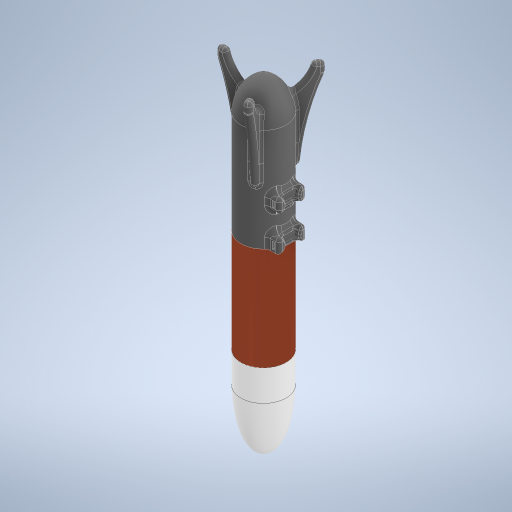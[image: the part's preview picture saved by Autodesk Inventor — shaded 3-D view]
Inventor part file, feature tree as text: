
AUTODESK INVENTOR PART (.ipt)
format: ipt  version: 2023 (Build 270158030, 158C)  size: 1,821,184 bytes
history: native  units: mm
features: fillet x17, sketch x15, extrude x14, other x12, plane x4, revolve x3, pattern_circular x2, pattern_linear x1, mirror x1, chamfer x1
ambient origin geometry x8: Origin, YZ Plane, XZ Plane, XY Plane, X Axis, Y Axis, Z Axis, Center Point
bodies: Body1 (feature_tree), Body2 (feature_tree), Body3 (feature_tree), Body4 (feature_tree), Body5 (feature_tree), Body6 (feature_tree), Body7 (feature_tree)
feature tree (70):
  other  "stage-one"
  extrude  "body-tube"  Depth=3.0mm
  extrude  "Extrusion2"  Depth=20.0mm
  extrude  "Extrusion3"  Depth=10.0mm
  plane  "Work Plane2"
  plane  "Work Plane4"
  extrude  "Extrusion4"  Depth=12.5mm
  plane  "Work Plane6"
  pattern_linear  "Rectangular Pattern1"  Count1=2  [1 undecoded]
  extrude  "Extrusion7"  Depth=6.0mm
  other  "Work Point2"
  revolve  "Revolution2"  [1 undecoded]
  mirror  "Mirror1"
  extrude  "Extrusion5"  Depth=4.0mm
  fillet  "Fillet1"  [1 undecoded]
  fillet  "Fillet2"  Radius=30.0mm
  fillet  "Fillet3"  Radius=200.0mm
  chamfer  "Chamfer1"  Distance=20.0mm
  fillet  "Fillet4"  Radius=7.0mm
  fillet  "Fillet5"  Radius=7.0mm
  fillet  "Fillet6"  Radius=5.0mm
  extrude  "Extrusion6"  Depth=2.0mm TaperAngle=45.0deg
  extrude  "fin 1 extrude"  Depth=5.0mm
  pattern_circular  "Circular Pattern1"  [2 undecoded]
  fillet  "Fillet7"  Radius=8.0mm
  fillet  "Fillet9"  Radius=10.0mm
  fillet  "Fillet10"  Radius=3.5mm
  fillet  "Fillet11"  [1 undecoded]
  fillet  "Fillet12"  Radius=1.0mm
  fillet  "Fillet13"  Radius=50.0mm
  extrude  "Extrusion9"  Depth=200.0mm
  extrude  "Extrusion10"  TaperAngle=90.0deg  [1 undecoded]
  extrude  "Extrusion11"  Depth=48.0mm
  extrude  "Extrusion12"  Depth=5.0mm
  other  "Work Point3"
  fillet  "Fillet15"  Radius=65.0mm
  fillet  "Fillet16"  Radius=15.0mm
  plane  "Work Plane7"
  extrude  "Extrusion14"  Depth=5.0mm
  revolve  "Revolution4"  [1 undecoded]
  fillet  "Fillet18"  Radius=126.0mm
  fillet  "Fillet19"  Radius=404.0mm
  fillet  "Fillet20"  Radius=150.0mm
  pattern_circular  "Circular Pattern2"  [2 undecoded]
  revolve  "Revolution3"  [1 undecoded]
  extrude  "Extrusion13"  Depth=5.0mm
  sketch  "Sketch1"  dims[d0=60.0mm d1=3.0mm]
  other  "rail-clamp-A"
  sketch  "Sketch5"  dims[d2=150.0mm d3=0.0mm d19=20.0mm]
  sketch  "Sketch6"  dims[d20=20.0mm d22=10.0mm]
  other  "Holding Bar"
  sketch  "Sketch8"  dims[d23=20.0mm d24=0.0mm d26=12.5mm]
  other  "bar-vertical"
  other  "Pattern of Holding Bar:1"
  other  "bar-angled"
  sketch  "Sketch9"  dims[d27=12.5mm]
  sketch  "Sketch10"  dims[d28=15.0mm]
  sketch  "Sketch11"  dims[d29=17.0mm]
  sketch  "Sketch12"  dims[d30=17.0mm]
  sketch  "Sketch13"  dims[d31=3.490659mm]
  sketch  "Sketch14"  dims[d33=3.490659mm]
  other  "stage-two"
  sketch  "Sketch15"  dims[d34=53.0mm d35=20.0mm]
  sketch  "Sketch16"  dims[d36=6.0mm d37=6.0mm]
  sketch  "Sketch17"  dims[d38=7.5mm d39=0.0mm d40=30.0mm]
  other  "nose-cone"
  sketch  "Sketch19"  dims[d41=53.296162mm d42=4.0mm]
  other  "drumsticks"
  sketch  "Sketch20"  dims[d43=200.0mm d44=100.0mm d45=0.0mm d46=0.0mm d47=90.0deg d49=30.0mm d50=200.0mm d51=100.0mm d52=0.0mm d53=0.0mm d56=20.0mm d58=50.0mm d59=7.0mm d60=7.0mm d61=5.0mm d62=2.0mm d63=2.0mm d64=45.0deg d65=5.0mm d66=5.0mm d67=8.0mm d68=10.0mm d70=3.5mm d76=0.0mm d77=0.0mm d78=1.0mm d79=50.0mm d80=0.0mm d85=53.0mm d86=52.992097mm d88=3.0mm d89=3.0mm d90=54.0mm d91=200.0mm d92=90.0deg d93=48.0mm d94=5.0mm d95=65.0mm d96=15.0mm d97=5.0mm d98=367.0mm d99=126.0mm d100=404.0mm d101=150.0mm d102=10.0mm d103=0.0mm d104=5.0mm d106=5.0mm d107=30.0mm d108=360.0deg d110=5.0mm d111=5.0mm d112=5.0mm d113=5.0mm d115=3.0mm d116=1.5mm d117=50.0mm d118=0.0mm d119=150.0mm d120=0.0mm d121=1.5mm d122=49.0mm d123=0.0mm d124=1.5mm d125=30.0mm d126=0.0mm d131=360.0deg d132=1.5mm d133=25.0mm d134=0.0mm d135=3.0mm d136=2.5mm d137=10.0mm d138=2.0mm d139=1.5mm d140=-110.0mm d141=15.0mm d142=400.0mm d143=0.0mm d144=15.0mm d145=0.0mm d147=19.0mm d148=15.0mm d149=410.0mm d150=7.5mm d151=13.0mm d152=10.5mm d153=2.25mm d154=2.25mm d159=3.85mm d160=3.85mm d161=50.0mm d162=2.0mm d163=50.0mm d164=339.5mm d165=360.0deg d166=5.0mm d167=3.0mm d168=10.0mm d169=80.0mm d170=360.0deg d184=3.0mm d189=128.5mm d190=4.8mm d191=3.35mm d192=30.0mm d193=28.0mm d194=7.0mm d195=7.0mm d196=45.0mm d197=75.0mm d198=78.0mm d200=1.5mm]
  other  "stick"
note: 11 required parameter values undecoded (feature->parameter linkage not recoverable at this tier; creation-order binding heuristic only, values carry confidence <= 0.55)